SOLIDWORKS PART (.sldprt)
format: sldprt  version: not decoded by parser v0  size: 128,000 bytes
history: native  units: mm
features: sketch x3, plane x2, extrude x2, material x1, cut_extrude x1 (+13 scaffold rows collapsed)
feature tree (22):
  scaffold x13  (default folders/planes/origin — collapsed)
  material  "ABS"
  plane  "Plane1"
  sketch  "Sketch1"  dims[c1.D2=2.008mm c1.D1=2.008mm c2.D2=2.0mm c2.D3=0.992mm c2.D4=39.0mm c2.D1=0.508mm]
  extrude  "Boss-Extrude1"  Depth=0.508mm
  sketch  "Sketch2"  dims[D1=0.508mm D2=1.27mm]
  extrude  "Boss-Extrude2"  Depth=38.1mm
  plane  "Plane2"
  sketch  "Sketch3"  dims[D1=7.62mm]
  cut_extrude  "Cut-Extrude1"  [1 undecoded]
decode coverage: 5 of 6 modeling features carry decoded parameters
note: 1 parameter value undecoded
note: suppression state not decoded; provenance and decode notes live in map.json
